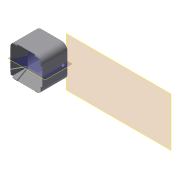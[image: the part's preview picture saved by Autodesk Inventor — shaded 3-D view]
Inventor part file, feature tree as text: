
AUTODESK INVENTOR PART (.ipt)
format: ipt  version: 2019.4 (Build 234330000, 330)  size: 204,288 bytes
history: native  units: mm
features: extrude x4, sketch x4, other x4, reference x3, plane x2, projected_geometry x2, pattern_circular x1, fillet x1
ambient origin geometry x8: Origin, YZ Plane, XZ Plane, XY Plane, X Axis, Y Axis, Z Axis, Center Point
bodies: Solid1 (feature_tree)
feature tree (21):
  plane  "Work Plane1"
  extrude  "Extrusion1"  Depth=12.0mm TaperAngle=0.0deg
  extrude  "Extrusion2"  Depth=27.0mm
  extrude  "Extrusion4"  Depth=5.0mm TaperAngle=0.0deg
  pattern_circular  "Circular Pattern1"  Count=4 Angle=360.0deg
  fillet  "Fillet1"  Radius=5.0mm
  plane  "Work Plane2"
  extrude  "Extrusion5"  Depth=6.0mm
  sketch  "Sketch1"  dims[d0=0.5mm d2=12.0mm d3=0.0mm]
  reference  "Reference1"
  reference  "Reference2"
  sketch  "Sketch2"  dims[d4=27.0mm d5=27.0mm]
  projected_geometry  "Projected Loop1"
  sketch  "Sketch4"  dims[d6=10.0mm d7=0.0mm d13=1.0mm d14=0.0mm d15=40.0mm d16=360.0deg d18=5.0mm]
  reference  "Reference5"
  projected_geometry  "Projected Loop4"
  sketch  "Sketch5"  dims[d19=6.0mm d20=6.0mm d21=2.8mm d22=2.8mm d23=0.0mm]
  other  "Assembly_Opentrons_Autofocus_v2.iam"
  other  "00_objectivelens_10x:1"
  other  "01_Slide_camera_v1:1"
  other  "00_LED_neopixel_single:1"
